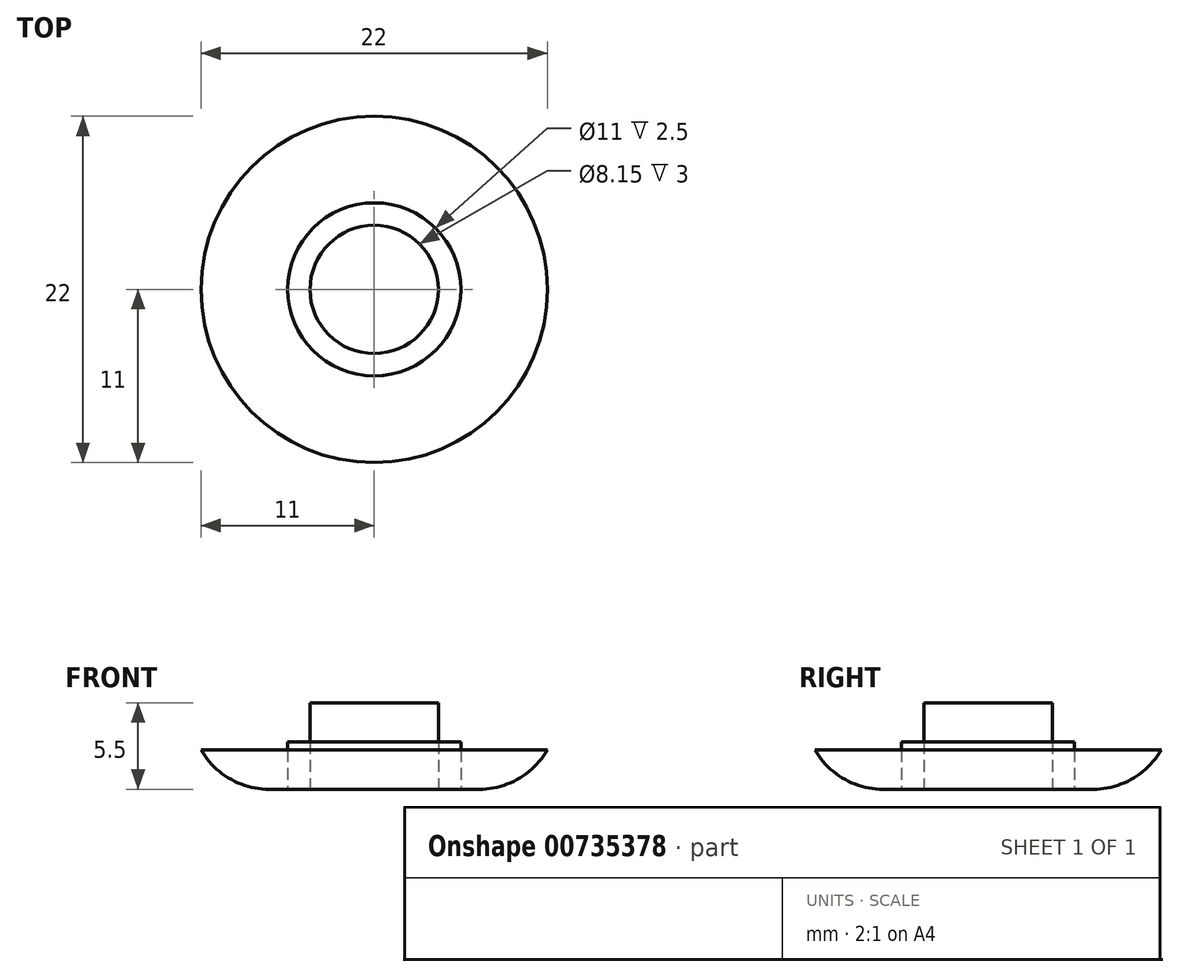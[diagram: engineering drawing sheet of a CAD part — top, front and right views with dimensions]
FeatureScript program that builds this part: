
annotation { "Feature Type Name" : "Feature", "Feature Type Description" : "" }
export const myFeature = defineFeature(function(context is Context, id is Id, definition is map)
    precondition{}
    {
        {
            var Q0;
            Q0=qCreatedBy(makeId("Top.planeOp"),FACE);
            var sketch = newSketch(context, id + "F0", { "sketchPlane" : qUnion([Q0])});
            skCircle(sketch, "E0", {"center": v(0, 0) * mm, "radius": 11 * mm});
            skCircle(sketch, "E1", {"center": v(0, 0) * mm, "radius": 5.5 * mm});
            skCircle(sketch, "E2", {"center": v(0, 0) * mm, "radius": 4.08 * mm});
            skSolve(sketch);
        }
        {
            var Q0;
            Q0=makeQuery(id+"F0.imprint","IMPRINT",FACE,{"disambiguationData":[TD([[makeQuery(id+"F0.imprint","IMPRINT",EDGE,{"derivedFrom":sQuery(id+"F0.wireOp",EDGE,"E2")}),1.0]])]});
            extrude(context, id + "F1", {"entities" : qUnion([Q0]), "depth" : 5.5 * mm, "offsetDistance" : 25 * mm});
        }
        {
            var Q0;
            Q0 = qSketchRegion(id + "F0", true);
            extrude(context, id + "F2", {"entities" : qUnion([Q0]), "depth" : 2.5 * mm, "offsetDistance" : 25 * mm});
        }
        {
            var Q0;
            Q0=makeQuery(id+"F0.imprint","IMPRINT",FACE,{"disambiguationData":[TD([[makeQuery(id+"F0.imprint","IMPRINT",EDGE,{"derivedFrom":sQuery(id+"F0.wireOp",EDGE,"E1")}),1.0]])]});
            extrude(context, id + "F3", {"entities" : qUnion([Q0]), "depth" : 3 * mm, "offsetDistance" : 25 * mm});
        }
        {
            var Q0;
            Q0=makeQuery(id+"F2.opExtrude","CAP_EDGE",EDGE,{"disambiguationData":[OSD([sQuery(id+"F0.wireOp",EDGE,"E0")])],"isStart":true});
            fillet(context, id + "F4", {"entities" : qUnion([Q0]), "radius" : 5 * mm, "tangentPropagation" : true, "allowEdgeOverflow" : false});
        }
    });
